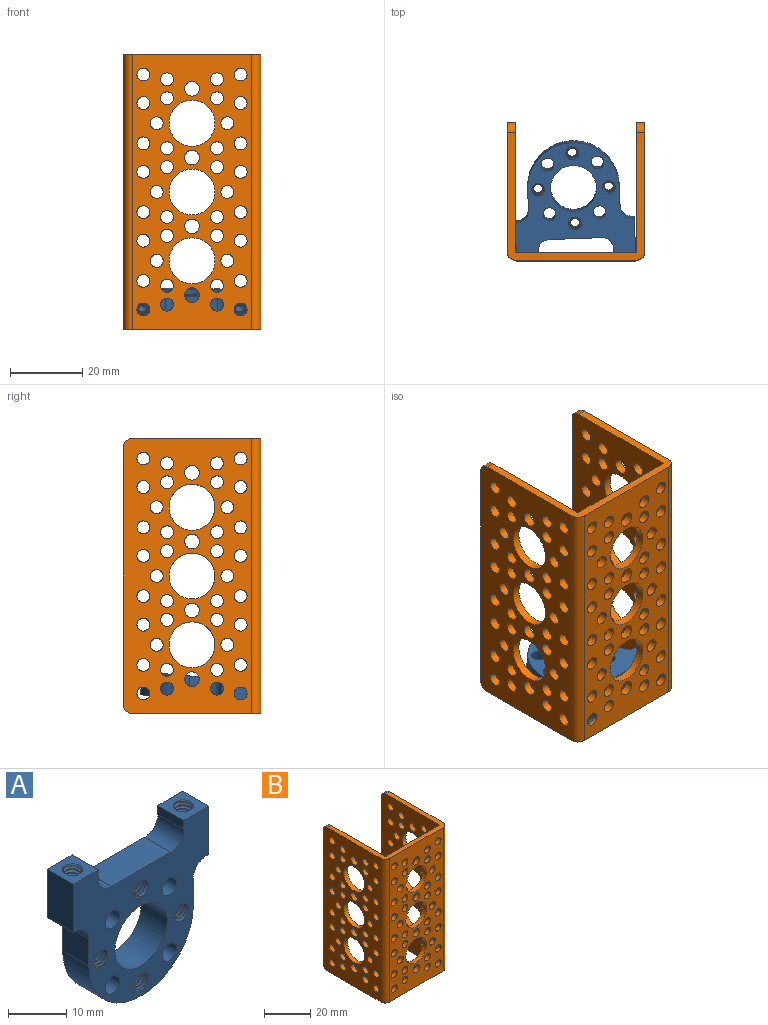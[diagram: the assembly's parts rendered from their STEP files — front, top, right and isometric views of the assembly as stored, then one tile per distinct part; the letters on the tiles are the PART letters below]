
ASSEMBLY  parts=2 mates=1
PART A: 77 faces, bbox 33x6.8x32 mm
  f0: cylinder r=1.75mm len=6.35mm, axis (0,-1,0), area 8.7mm2, adj f46,f47,f75,f76
  f1: cylinder r=1.75mm len=6.35mm, axis (0,-1,0), area 8.7mm2, adj f46,f47,f73,f74
  f2: cylinder r=1.75mm len=6.35mm, axis (0,-1,0), area 8.7mm2, adj f46,f47,f71,f72
  f3: cylinder r=1.75mm len=6.54mm, axis (0,0,-1), area 9mm2, adj f54,f68,f69,f70
  f4: cylinder r=1.75mm len=6.54mm, axis (0,0,-1), area 9mm2, adj f50,f65,f66,f67
  f5: cylinder r=1.75mm len=6.35mm, axis (0,-1,0), area 8.7mm2, adj f46,f47,f63,f64
  f6: cylinder r=1.35mm len=2.71mm, axis (0,0,1), area 7.6mm2, adj f7,f15,f68,f69,f70
  f7: cylinder r=1.35mm len=2.71mm, axis (0,0,1), area 2mm2, adj f6,f8,f69,f70
  f8: cylinder r=1.35mm len=2.71mm, axis (0,0,1), area 2mm2, adj f7,f9,f69,f70
  f9: cylinder r=1.35mm len=2.71mm, axis (0,0,1), area 2mm2, adj f8,f10,f69,f70
  f10: cylinder r=1.35mm len=2.71mm, axis (0,0,1), area 2mm2, adj f9,f11,f69,f70
  f11: cylinder r=1.35mm len=2.71mm, axis (0,0,1), area 2mm2, adj f10,f12,f69,f70
  f12: cylinder r=1.35mm len=2.71mm, axis (0,0,1), area 2mm2, adj f11,f13,f69,f70
  f13: cylinder r=1.35mm len=2.71mm, axis (0,0,1), area 2mm2, adj f12,f14,f69,f70
  f14: cylinder r=1.35mm len=2.71mm, axis (0,0,1), area 1.3mm2, adj f13,f39,f69,f70
  f15: cone r=1.35mm half-angle=59deg, axis (0,0,1), area 6.7mm2, adj f6
  f16: cylinder r=1.35mm len=2.71mm, axis (0,0,1), area 7.6mm2, adj f17,f25,f65,f66,f67
  f17: cylinder r=1.35mm len=2.71mm, axis (0,0,1), area 2mm2, adj f16,f18,f66,f67
  f18: cylinder r=1.35mm len=2.71mm, axis (0,0,1), area 2mm2, adj f17,f19,f66,f67
  f19: cylinder r=1.35mm len=2.71mm, axis (0,0,1), area 2mm2, adj f18,f20,f66,f67
  f20: cylinder r=1.35mm len=2.71mm, axis (0,0,1), area 2mm2, adj f19,f21,f66,f67
  f21: cylinder r=1.35mm len=2.71mm, axis (0,0,1), area 2mm2, adj f20,f22,f66,f67
  f22: cylinder r=1.35mm len=2.71mm, axis (0,0,1), area 2mm2, adj f21,f23,f66,f67
  f23: cylinder r=1.35mm len=2.71mm, axis (0,0,1), area 2mm2, adj f22,f24,f66,f67
  f24: cylinder r=1.35mm len=2.71mm, axis (0,0,1), area 1.3mm2, adj f23,f38,f66,f67
  f25: cone r=1.35mm half-angle=59deg, axis (0,0,1), area 6.7mm2, adj f16
  f26: cylinder r=1.78mm len=6.35mm, axis (0,1,0), area 70.9mm2, adj f46,f47
  f27: cylinder r=1.78mm len=6.35mm, axis (0,1,0), area 70.9mm2, adj f46,f47
  f28: cylinder r=1.78mm len=6.35mm, axis (0,1,0), area 70.9mm2, adj f46,f47
  f29: cylinder r=1.78mm len=6.35mm, axis (0,1,0), area 70.9mm2, adj f46,f47
  f30: cylinder r=1.35mm len=5.55mm, axis (0,1,0), area 13.8mm2, adj f44,f45,f75,f76
  f31: cylinder r=1.35mm len=5.55mm, axis (0,1,0), area 13.8mm2, adj f42,f43,f73,f74
  f32: cylinder r=1.35mm len=5.55mm, axis (0,1,0), area 13.8mm2, adj f40,f41,f71,f72
  f33: cylinder r=1.35mm len=5.55mm, axis (0,1,0), area 13.8mm2, adj f36,f37,f63,f64
  f34: cylinder r=6.36mm len=12.73mm, axis (0,1,0), area 253.9mm2, adj f46,f47
  f35: cylinder r=12.7mm len=25.4mm, axis (0,-1,0), area 253.4mm2, adj f46,f47,f57,f58
  f36: cone r=1.75mm half-angle=45deg, axis (0,-1,0), area 3.3mm2, adj f33,f47,f63,f64
  f37: cone r=1.35mm half-angle=45deg, axis (0,1,0), area 3.3mm2, adj f33,f46,f63,f64
  f38: cone r=1.35mm half-angle=45deg, axis (0,0,1), area 3.3mm2, adj f24,f50,f66,f67
  f39: cone r=1.35mm half-angle=45deg, axis (0,0,1), area 3.3mm2, adj f14,f54,f69,f70
  f40: cone r=1.75mm half-angle=45deg, axis (0,-1,0), area 3.3mm2, adj f32,f47,f71,f72
  f41: cone r=1.35mm half-angle=45deg, axis (0,1,0), area 3.3mm2, adj f32,f46,f71,f72
  f42: cone r=1.75mm half-angle=45deg, axis (0,-1,0), area 3.3mm2, adj f31,f47,f73,f74
  f43: cone r=1.35mm half-angle=45deg, axis (0,1,0), area 3.3mm2, adj f31,f46,f73,f74
  f44: cone r=1.75mm half-angle=45deg, axis (0,-1,0), area 3.3mm2, adj f30,f47,f75,f76
  f45: cone r=1.35mm half-angle=45deg, axis (0,1,0), area 3.3mm2, adj f30,f46,f75,f76
  f46: plane 33.02x31.75mm, normal (0,1,0), area 511.8mm2, adj f0,f1,f2,f5,f26,f27,f28,f29
  f47: plane 33.02x31.75mm, normal (0,-1,0), area 511.8mm2, adj f0,f1,f2,f5,f26,f27,f28,f29
  f48: plane 6.35x0.64mm, normal (0,0,-1), area 4mm2, adj f46,f47,f49,f60
  f49: plane 10.16x6.35mm, normal (1,0,0), area 64.5mm2, adj f46,f47,f48,f50
  f50: plane 6.35x6.08mm, normal (0,0,1), area 29mm2, adj f4,f38,f46,f47,f49,f51
  f51: plane 6.35x1.91mm, normal (-1,0,0), area 12.1mm2, adj f46,f47,f50,f61
  f52: plane 14.51x6.35mm, normal (0,0,1), area 92.1mm2, adj f46,f47,f61,f62
  f53: plane 6.35x1.91mm, normal (1,0,0), area 12.1mm2, adj f46,f47,f54,f62
  f54: plane 6.35x6.08mm, normal (0,0,1), area 29mm2, adj f3,f39,f46,f47,f53,f55
  f55: plane 10.16x6.35mm, normal (-1,0,0), area 64.5mm2, adj f46,f47,f54,f56
  f56: plane 6.35x0.64mm, normal (0,0,-1), area 4mm2, adj f46,f47,f55,f59
  f57: plane 6.35x5.72mm, normal (-1,0,0), area 36.3mm2, adj f35,f46,f47,f59
  f58: plane 6.35x5.72mm, normal (1,0,0), area 36.3mm2, adj f35,f46,f47,f60
  f59: cylinder r=3.17mm len=6.35mm, axis (0,-1,0), area 31.7mm2, adj f46,f47,f56,f57
  f60: cylinder r=3.17mm len=6.35mm, axis (0,-1,0), area 31.7mm2, adj f46,f47,f48,f58
  f61: cylinder r=3.17mm len=6.35mm, axis (0,-1,0), area 31.7mm2, adj f46,f47,f51,f52
  f62: cylinder r=3.17mm len=6.35mm, axis (0,-1,0), area 31.7mm2, adj f46,f47,f52,f53
  f63: bspline ~6.58x3.5mm, area 34mm2, adj f5,f33,f36,f37
  f64: bspline ~6.58x3.5mm, area 34mm2, adj f5,f33,f36,f37
  f65: cone r=0.98mm half-angle=55deg, axis (0,0,1), area 1.9mm2, adj f4,f16,f66,f67
  f66: bspline ~7.28x3.49mm, area 36.9mm2, adj f4,f16,f17,f18,f19,f20,f21,f22
  f67: bspline ~6.82x3.5mm, area 36.9mm2, adj f4,f16,f17,f18,f19,f20,f21,f22
  f68: cone r=0.98mm half-angle=55deg, axis (0,0,1), area 1.9mm2, adj f3,f6,f69,f70
  f69: bspline ~7.28x3.49mm, area 36.9mm2, adj f3,f6,f7,f8,f9,f10,f11,f12
  f70: bspline ~6.82x3.5mm, area 36.9mm2, adj f3,f6,f7,f8,f9,f10,f11,f12
  f71: bspline ~6.58x3.5mm, area 34mm2, adj f2,f32,f40,f41
  f72: bspline ~6.58x3.5mm, area 34mm2, adj f2,f32,f40,f41
  f73: bspline ~6.58x3.5mm, area 34mm2, adj f1,f31,f42,f43
  f74: bspline ~6.58x3.5mm, area 34mm2, adj f1,f31,f42,f43
  f75: bspline ~6.58x3.5mm, area 34mm2, adj f0,f30,f44,f45
  f76: bspline ~6.58x3.5mm, area 34mm2, adj f0,f30,f44,f45
PART B: 151 faces, bbox 38.1x38.1x76.2 mm
  f0: cylinder r=1.78mm len=3.56mm, axis (0,-1,0), area 25.5mm2, adj f135,f139
  f1: cylinder r=1.78mm len=3.56mm, axis (0,-1,0), area 25.5mm2, adj f135,f139
  f2: cylinder r=1.78mm len=3.56mm, axis (0,-1,0), area 25.5mm2, adj f135,f139
  f3: cylinder r=1.78mm len=3.56mm, axis (0,-1,0), area 25.5mm2, adj f135,f139
  f4: cylinder r=1.78mm len=3.56mm, axis (0,-1,0), area 25.5mm2, adj f135,f139
  f5: cylinder r=1.78mm len=3.56mm, axis (0,-1,0), area 25.5mm2, adj f135,f139
  f6: cylinder r=1.78mm len=3.56mm, axis (0,-1,0), area 25.5mm2, adj f135,f139
  f7: cylinder r=1.78mm len=3.56mm, axis (0,-1,0), area 25.5mm2, adj f135,f139
  f8: cylinder r=1.78mm len=3.56mm, axis (0,-1,0), area 25.5mm2, adj f135,f139
  f9: cylinder r=1.78mm len=3.56mm, axis (0,-1,0), area 25.5mm2, adj f135,f139
  f10: cylinder r=2.03mm len=4.06mm, axis (0,-1,0), area 29.2mm2, adj f135,f139
  f11: cylinder r=2.03mm len=4.06mm, axis (0,-1,0), area 29.2mm2, adj f135,f139
  f12: cylinder r=1.78mm len=3.56mm, axis (0,-1,0), area 25.5mm2, adj f135,f139
  f13: cylinder r=1.78mm len=3.56mm, axis (0,-1,0), area 25.5mm2, adj f135,f139
  f14: cylinder r=1.78mm len=3.56mm, axis (0,-1,0), area 25.5mm2, adj f135,f139
  f15: cylinder r=1.78mm len=3.56mm, axis (0,-1,0), area 25.5mm2, adj f135,f139
  f16: cylinder r=1.78mm len=3.56mm, axis (0,-1,0), area 25.5mm2, adj f135,f139
  f17: cylinder r=1.78mm len=3.56mm, axis (0,-1,0), area 25.5mm2, adj f135,f139
  f18: cylinder r=1.78mm len=3.56mm, axis (0,-1,0), area 25.5mm2, adj f135,f139
  f19: cylinder r=1.78mm len=3.56mm, axis (0,-1,0), area 25.5mm2, adj f135,f139
  f20: cylinder r=1.78mm len=3.56mm, axis (0,-1,0), area 25.5mm2, adj f135,f139
  f21: cylinder r=1.78mm len=3.56mm, axis (0,-1,0), area 25.5mm2, adj f135,f139
  f22: cylinder r=6.36mm len=12.73mm, axis (0,-1,0), area 91.4mm2, adj f135,f139
  f23: cylinder r=6.36mm len=12.73mm, axis (0,-1,0), area 91.4mm2, adj f135,f139
  f24: cylinder r=1.78mm len=3.56mm, axis (0,-1,0), area 25.5mm2, adj f135,f139
  f25: cylinder r=1.78mm len=3.56mm, axis (0,-1,0), area 25.5mm2, adj f135,f139
  f26: cylinder r=1.78mm len=3.56mm, axis (0,-1,0), area 25.5mm2, adj f135,f139
  f27: cylinder r=1.78mm len=3.56mm, axis (0,-1,0), area 25.5mm2, adj f135,f139
  f28: cylinder r=1.78mm len=3.56mm, axis (0,-1,0), area 25.5mm2, adj f135,f139
  f29: cylinder r=1.78mm len=3.56mm, axis (0,-1,0), area 25.5mm2, adj f135,f139
  f30: cylinder r=1.78mm len=3.56mm, axis (0,-1,0), area 25.5mm2, adj f135,f139
  f31: cylinder r=1.78mm len=3.56mm, axis (0,-1,0), area 25.5mm2, adj f135,f139
  f32: cylinder r=1.78mm len=3.56mm, axis (0,-1,0), area 25.5mm2, adj f135,f139
  f33: cylinder r=1.78mm len=3.56mm, axis (0,-1,0), area 25.5mm2, adj f135,f139
  f34: cylinder r=1.78mm len=3.56mm, axis (0,-1,0), area 25.5mm2, adj f135,f139
  f35: cylinder r=1.78mm len=3.56mm, axis (0,-1,0), area 25.5mm2, adj f135,f139
  f36: cylinder r=2.03mm len=4.06mm, axis (0,-1,0), area 29.2mm2, adj f135,f139
  f37: cylinder r=2.03mm len=4.06mm, axis (0,-1,0), area 29.2mm2, adj f135,f139
  f38: cylinder r=1.78mm len=3.56mm, axis (0,-1,0), area 25.5mm2, adj f135,f139
  f39: cylinder r=1.78mm len=3.56mm, axis (0,-1,0), area 25.5mm2, adj f135,f139
  f40: cylinder r=1.78mm len=3.56mm, axis (0,-1,0), area 25.5mm2, adj f135,f139
  f41: cylinder r=1.78mm len=3.56mm, axis (0,-1,0), area 25.5mm2, adj f135,f139
  f42: cylinder r=1.78mm len=3.56mm, axis (0,-1,0), area 25.5mm2, adj f135,f139
  f43: cylinder r=1.78mm len=3.56mm, axis (0,-1,0), area 25.5mm2, adj f135,f139
  f44: cylinder r=6.36mm len=12.73mm, axis (0,-1,0), area 91.4mm2, adj f135,f139
  f45: cylinder r=2.03mm len=4.06mm, axis (1,0,0), area 29.2mm2, adj f136,f138
  f46: cylinder r=2.03mm len=4.06mm, axis (1,0,0), area 29.2mm2, adj f140,f142
  f47: cylinder r=1.78mm len=3.56mm, axis (1,0,0), area 25.5mm2, adj f136,f138
  f48: cylinder r=1.78mm len=3.56mm, axis (1,0,0), area 25.5mm2, adj f140,f142
  f49: cylinder r=1.78mm len=3.56mm, axis (1,0,0), area 25.5mm2, adj f136,f138
  f50: cylinder r=1.78mm len=3.56mm, axis (1,0,0), area 25.5mm2, adj f140,f142
  f51: cylinder r=1.78mm len=3.56mm, axis (1,0,0), area 25.5mm2, adj f136,f138
  f52: cylinder r=1.78mm len=3.56mm, axis (1,0,0), area 25.5mm2, adj f140,f142
  f53: cylinder r=1.78mm len=3.56mm, axis (1,0,0), area 25.5mm2, adj f136,f138
  f54: cylinder r=1.78mm len=3.56mm, axis (1,0,0), area 25.5mm2, adj f140,f142
  f55: cylinder r=1.78mm len=3.56mm, axis (1,0,0), area 25.5mm2, adj f136,f138
  f56: cylinder r=1.78mm len=3.56mm, axis (1,0,0), area 25.5mm2, adj f140,f142
  f57: cylinder r=1.78mm len=3.56mm, axis (1,0,0), area 25.5mm2, adj f136,f138
  f58: cylinder r=1.78mm len=3.56mm, axis (1,0,0), area 25.5mm2, adj f140,f142
  f59: cylinder r=1.78mm len=3.56mm, axis (1,0,0), area 25.5mm2, adj f136,f138
  f60: cylinder r=1.78mm len=3.56mm, axis (1,0,0), area 25.5mm2, adj f140,f142
  f61: cylinder r=1.78mm len=3.56mm, axis (1,0,0), area 25.5mm2, adj f136,f138
  f62: cylinder r=1.78mm len=3.56mm, axis (1,0,0), area 25.5mm2, adj f140,f142
  f63: cylinder r=1.78mm len=3.56mm, axis (1,0,0), area 25.5mm2, adj f136,f138
  f64: cylinder r=1.78mm len=3.56mm, axis (1,0,0), area 25.5mm2, adj f140,f142
  f65: cylinder r=1.78mm len=3.56mm, axis (1,0,0), area 25.5mm2, adj f136,f138
  f66: cylinder r=1.78mm len=3.56mm, axis (1,0,0), area 25.5mm2, adj f140,f142
  f67: cylinder r=1.78mm len=3.56mm, axis (1,0,0), area 25.5mm2, adj f136,f138
  f68: cylinder r=1.78mm len=3.56mm, axis (1,0,0), area 25.5mm2, adj f140,f142
  f69: cylinder r=1.78mm len=3.56mm, axis (1,0,0), area 25.5mm2, adj f136,f138
  f70: cylinder r=1.78mm len=3.56mm, axis (1,0,0), area 25.5mm2, adj f140,f142
  f71: cylinder r=1.78mm len=3.56mm, axis (1,0,0), area 25.5mm2, adj f136,f138
  f72: cylinder r=1.78mm len=3.56mm, axis (1,0,0), area 25.5mm2, adj f140,f142
  f73: cylinder r=1.78mm len=3.56mm, axis (1,0,0), area 25.5mm2, adj f136,f138
  f74: cylinder r=1.78mm len=3.56mm, axis (1,0,0), area 25.5mm2, adj f140,f142
  f75: cylinder r=1.78mm len=3.56mm, axis (1,0,0), area 25.5mm2, adj f136,f138
  f76: cylinder r=1.78mm len=3.56mm, axis (1,0,0), area 25.5mm2, adj f140,f142
  f77: cylinder r=1.78mm len=3.56mm, axis (1,0,0), area 25.5mm2, adj f136,f138
  f78: cylinder r=1.78mm len=3.56mm, axis (1,0,0), area 25.5mm2, adj f140,f142
  f79: cylinder r=2.03mm len=4.06mm, axis (1,0,0), area 29.2mm2, adj f136,f138
  f80: cylinder r=2.03mm len=4.06mm, axis (1,0,0), area 29.2mm2, adj f140,f142
  f81: cylinder r=1.78mm len=3.56mm, axis (1,0,0), area 25.5mm2, adj f136,f138
  f82: cylinder r=1.78mm len=3.56mm, axis (1,0,0), area 25.5mm2, adj f140,f142
  f83: cylinder r=1.78mm len=3.56mm, axis (1,0,0), area 25.5mm2, adj f136,f138
  f84: cylinder r=1.78mm len=3.56mm, axis (1,0,0), area 25.5mm2, adj f140,f142
  f85: cylinder r=1.78mm len=3.56mm, axis (1,0,0), area 25.5mm2, adj f136,f138
  f86: cylinder r=1.78mm len=3.56mm, axis (1,0,0), area 25.5mm2, adj f140,f142
  f87: cylinder r=1.78mm len=3.56mm, axis (1,0,0), area 25.5mm2, adj f136,f138
  f88: cylinder r=1.78mm len=3.56mm, axis (1,0,0), area 25.5mm2, adj f140,f142
  f89: cylinder r=1.78mm len=3.56mm, axis (1,0,0), area 25.5mm2, adj f136,f138
  f90: cylinder r=1.78mm len=3.56mm, axis (1,0,0), area 25.5mm2, adj f140,f142
  f91: cylinder r=1.78mm len=3.56mm, axis (1,0,0), area 25.5mm2, adj f136,f138
  f92: cylinder r=1.78mm len=3.56mm, axis (1,0,0), area 25.5mm2, adj f140,f142
  f93: cylinder r=1.78mm len=3.56mm, axis (1,0,0), area 25.5mm2, adj f136,f138
  f94: cylinder r=1.78mm len=3.56mm, axis (1,0,0), area 25.5mm2, adj f140,f142
  f95: cylinder r=1.78mm len=3.56mm, axis (1,0,0), area 25.5mm2, adj f136,f138
  f96: cylinder r=1.78mm len=3.56mm, axis (1,0,0), area 25.5mm2, adj f140,f142
  f97: cylinder r=1.78mm len=3.56mm, axis (1,0,0), area 25.5mm2, adj f136,f138
  f98: cylinder r=1.78mm len=3.56mm, axis (1,0,0), area 25.5mm2, adj f140,f142
  f99: cylinder r=1.78mm len=3.56mm, axis (1,0,0), area 25.5mm2, adj f136,f138
  f100: cylinder r=1.78mm len=3.56mm, axis (1,0,0), area 25.5mm2, adj f140,f142
  f101: cylinder r=1.78mm len=3.56mm, axis (1,0,0), area 25.5mm2, adj f136,f138
  f102: cylinder r=1.78mm len=3.56mm, axis (1,0,0), area 25.5mm2, adj f140,f142
  f103: cylinder r=1.78mm len=3.56mm, axis (1,0,0), area 25.5mm2, adj f136,f138
  f104: cylinder r=1.78mm len=3.56mm, axis (1,0,0), area 25.5mm2, adj f140,f142
  f105: cylinder r=6.36mm len=12.73mm, axis (1,0,0), area 91.4mm2, adj f140,f142
  f106: cylinder r=6.36mm len=12.73mm, axis (1,0,0), area 91.4mm2, adj f140,f142
  f107: cylinder r=6.36mm len=12.73mm, axis (1,0,0), area 91.4mm2, adj f136,f138
  f108: cylinder r=6.36mm len=12.73mm, axis (1,0,0), area 91.4mm2, adj f136,f138
  f109: cylinder r=1.78mm len=3.56mm, axis (1,0,0), area 25.5mm2, adj f136,f138
  f110: cylinder r=1.78mm len=3.56mm, axis (1,0,0), area 25.5mm2, adj f140,f142
  f111: cylinder r=1.78mm len=3.56mm, axis (1,0,0), area 25.5mm2, adj f136,f138
  f112: cylinder r=1.78mm len=3.56mm, axis (1,0,0), area 25.5mm2, adj f140,f142
  f113: cylinder r=1.78mm len=3.56mm, axis (1,0,0), area 25.5mm2, adj f136,f138
  f114: cylinder r=1.78mm len=3.56mm, axis (1,0,0), area 25.5mm2, adj f140,f142
  f115: cylinder r=1.78mm len=3.56mm, axis (1,0,0), area 25.5mm2, adj f136,f138
  f116: cylinder r=1.78mm len=3.56mm, axis (1,0,0), area 25.5mm2, adj f140,f142
  f117: cylinder r=2.03mm len=4.06mm, axis (1,0,0), area 29.2mm2, adj f136,f138
  f118: cylinder r=2.03mm len=4.06mm, axis (1,0,0), area 29.2mm2, adj f140,f142
  f119: cylinder r=2.03mm len=4.06mm, axis (1,0,0), area 29.2mm2, adj f136,f138
  f120: cylinder r=2.03mm len=4.06mm, axis (1,0,0), area 29.2mm2, adj f140,f142
  f121: cylinder r=1.78mm len=3.56mm, axis (1,0,0), area 25.5mm2, adj f136,f138
  f122: cylinder r=1.78mm len=3.56mm, axis (1,0,0), area 25.5mm2, adj f140,f142
  f123: cylinder r=1.78mm len=3.56mm, axis (1,0,0), area 25.5mm2, adj f136,f138
  f124: cylinder r=1.78mm len=3.56mm, axis (1,0,0), area 25.5mm2, adj f140,f142
  f125: cylinder r=1.78mm len=3.56mm, axis (1,0,0), area 25.5mm2, adj f136,f138
  f126: cylinder r=1.78mm len=3.56mm, axis (1,0,0), area 25.5mm2, adj f140,f142
  f127: cylinder r=1.78mm len=3.56mm, axis (1,0,0), area 25.5mm2, adj f136,f138
  f128: cylinder r=1.78mm len=3.56mm, axis (1,0,0), area 25.5mm2, adj f140,f142
  f129: cylinder r=1.78mm len=3.56mm, axis (1,0,0), area 25.5mm2, adj f136,f138
  f130: cylinder r=1.78mm len=3.56mm, axis (1,0,0), area 25.5mm2, adj f140,f142
  f131: cylinder r=1.78mm len=3.56mm, axis (1,0,0), area 25.5mm2, adj f136,f138
  f132: cylinder r=1.78mm len=3.56mm, axis (1,0,0), area 25.5mm2, adj f140,f142
  f133: cylinder r=6.36mm len=12.73mm, axis (1,0,0), area 91.4mm2, adj f136,f138
  f134: cylinder r=6.36mm len=12.73mm, axis (1,0,0), area 91.4mm2, adj f140,f142
  f135: plane 76.2x33.02mm, normal (0,-1,0), area 1705.3mm2, adj f0,f1,f2,f3,f4,f5,f6,f7
  f136: plane 76.2x35.56mm, normal (1,0,0), area 1896.1mm2, adj f45,f47,f49,f51,f53,f55,f57,f59
  f137: plane 71.12x2.29mm, normal (0,1,0), area 162.6mm2, adj f136,f138,f146,f150
  f138: plane 76.2x35.81mm, normal (-1,0,0), area 1915.4mm2, adj f45,f47,f49,f51,f53,f55,f57,f59
  f139: plane 76.2x33.53mm, normal (0,1,0), area 1744mm2, adj f0,f1,f2,f3,f4,f5,f6,f7
  f140: plane 76.2x35.81mm, normal (1,0,0), area 1915.4mm2, adj f46,f48,f50,f52,f54,f56,f58,f60
  f141: plane 71.12x2.29mm, normal (0,1,0), area 162.6mm2, adj f140,f142,f145,f149
  f142: plane 76.2x35.56mm, normal (-1,0,0), area 1896.1mm2, adj f46,f48,f50,f52,f54,f56,f58,f60
  f143: plane 38.1x35.56mm, normal (0,0,1), area 236.5mm2, adj f135,f136,f138,f139,f140,f142,f145,f146
  f144: plane 38.1x35.56mm, normal (0,0,-1), area 236.5mm2, adj f135,f136,f138,f139,f140,f142,f147,f148
  f145: cylinder r=2.54mm len=2.54mm, axis (-1,0,0), area 9.1mm2, adj f140,f141,f142,f143
  f146: cylinder r=2.54mm len=2.54mm, axis (-1,0,0), area 9.1mm2, adj f136,f137,f138,f143
  f147: cylinder r=2.54mm len=76.2mm, axis (0,0,-1), area 304mm2, adj f135,f142,f143,f144
  f148: cylinder r=2.54mm len=76.2mm, axis (0,0,-1), area 304mm2, adj f135,f136,f143,f144
  f149: cylinder r=2.54mm len=2.54mm, axis (1,0,0), area 9.1mm2, adj f140,f141,f142,f144
  f150: cylinder r=2.54mm len=2.54mm, axis (1,0,0), area 9.1mm2, adj f136,f137,f138,f144
PLACE A rot(axis=(1,0.02,0.02),95.2deg) t=(17.13,28.71,4.05)mm
PLACE B rot(axis=(0.31,-0.94,-0.15),0deg) t=(-1.21,8.04,-0.04)mm
MATE fastened A.f24 <-> B.f33  axis (0,-1,0) through (31.31,10.33,5.54)mm
